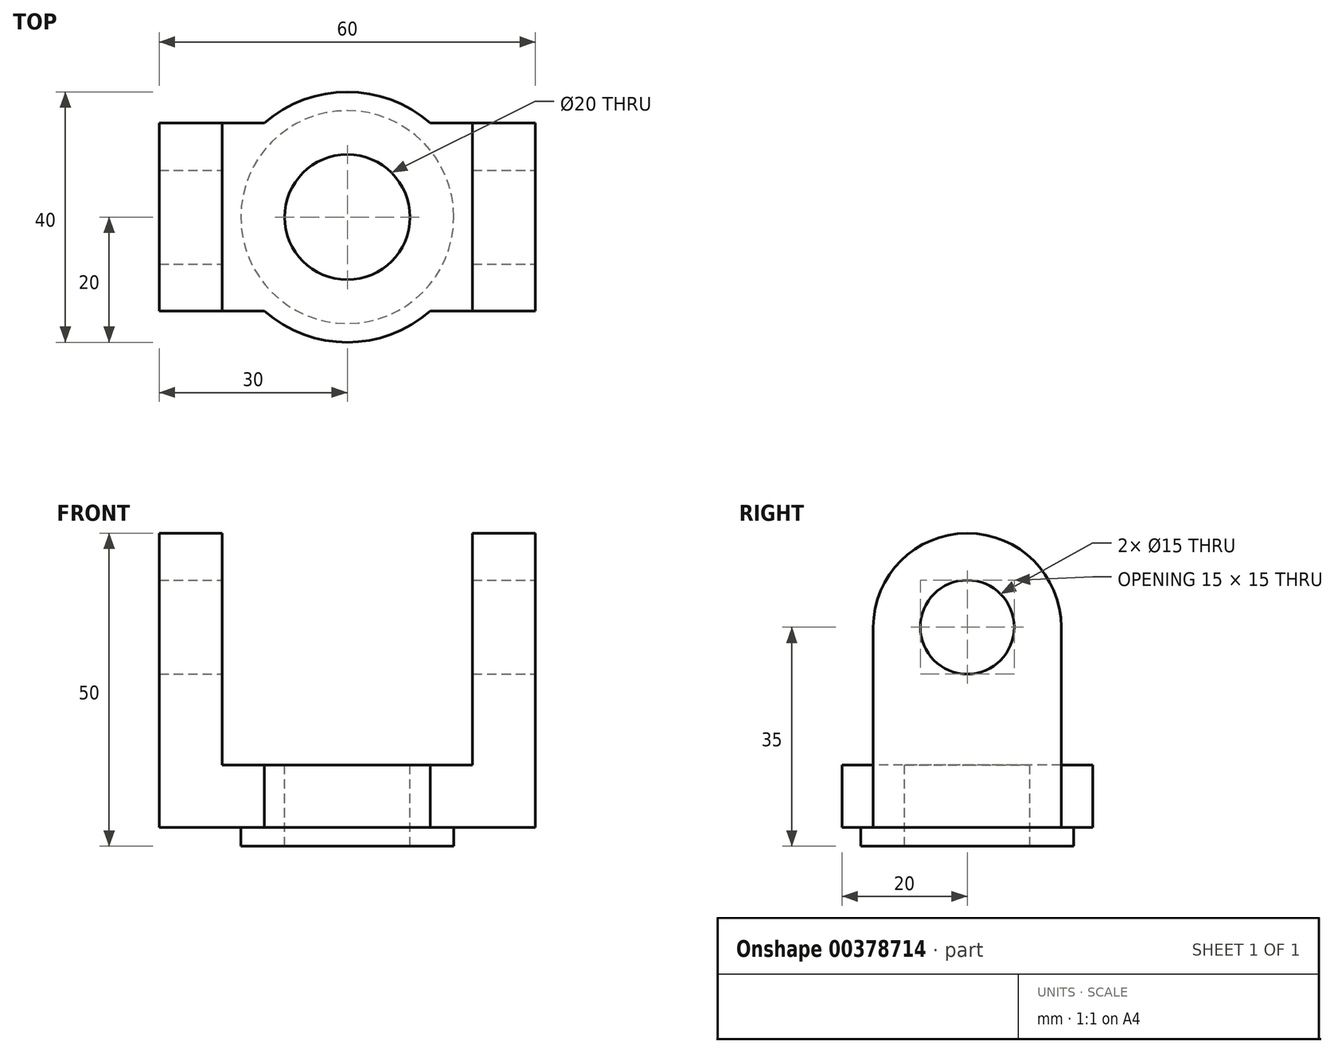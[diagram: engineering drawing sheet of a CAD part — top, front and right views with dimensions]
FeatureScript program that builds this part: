
annotation { "Feature Type Name" : "Feature", "Feature Type Description" : "" }
export const myFeature = defineFeature(function(context is Context, id is Id, definition is map)
    precondition{}
    {
        {
            var Q0;
            Q0=qCreatedBy(makeId("Top.planeOp"),FACE);
            var sketch = newSketch(context, id + "F0", { "sketchPlane" : qUnion([Q0])});
            skCircle(sketch, "E0", {"center": v(0, 0) * mm, "radius": 17 * mm});
            skSolve(sketch);
        }
        {
            var Q0;
            Q0 = qSketchRegion(id + "F0", true);
            extrude(context, id + "F1", {"entities" : qUnion([Q0]), "depth" : 3 * mm});
        }
        {
            var Q0;
            Q0=makeQuery(id+"F1.opExtrude","CAP_FACE",FACE,{"disambiguationData":[OSD([sQuery(id+"F0.wireOp",EDGE,"E0")])],"isStart":false});
            var sketch = newSketch(context, id + "F2", { "sketchPlane" : qUnion([Q0])});
            skLineSegment(sketch, "E1.bottom", {"start": v(-30, 15) * mm, "end": v(-13.23, 15) * mm});
            skLineSegment(sketch, "E1.top", {"start": v(-30, -15) * mm, "end": v(-13.23, -15) * mm});
            skLineSegment(sketch, "E1.left", {"start": v(-30, 15) * mm, "end": v(-30, -15) * mm});
            skLineSegment(sketch, "E1.right", {"start": v(30, 15) * mm, "end": v(30, -15) * mm});
            skLineSegment(sketch, "E2", {"start": v(0, 0) * mm, "end": v(0, 17) * mm, "construction": true});
            skLineSegment(sketch, "E3", {"start": v(0, 0) * mm, "end": v(17, 0) * mm, "construction": true});
            skArc(sketch, "E4", {"start": v(-13.23, -15) * mm, "mid": v(0, -20) * mm, "end": v(13.23, -15) * mm});
            skLineSegment(sketch, "E5.trimOffspring", {"start": v(13.23, 15) * mm, "end": v(30, 15) * mm});
            skLineSegment(sketch, "E6.trimOffspring", {"start": v(13.23, -15) * mm, "end": v(30, -15) * mm});
            skArc(sketch, "E7.trimOffspring", {"start": v(13.23, 15) * mm, "mid": v(0, 20) * mm, "end": v(-13.23, 15) * mm});
            skSolve(sketch);
        }
        {
            var Q0;
            Q0 = qSketchRegion(id + "F2", true);
            extrude(context, id + "F3", {"entities" : qUnion([Q0]), "operationType" : NewBodyOperationType.ADD, "depth" : 50 * mm});
        }
        {
            var Q0;
            Q0=makeQuery(id+"F3.opExtrude","SWEPT_FACE",FACE,{"disambiguationData":[OSD([sQuery(id+"F2.wireOp",EDGE,"E1.right")])]});
            var sketch = newSketch(context, id + "F4", { "sketchPlane" : qUnion([Q0])});
            skCircle(sketch, "E8", {"center": v(0, 35) * mm, "radius": 7.5 * mm});
            skArc(sketch, "E9", {"start": v(15, 35) * mm, "mid": v(0, 50) * mm, "end": v(-15, 35) * mm});
            skLineSegment(sketch, "E10", {"start": v(-15, 35) * mm, "end": v(-15, 53) * mm});
            skLineSegment(sketch, "E11", {"start": v(-15, 53) * mm, "end": v(15, 53) * mm});
            skLineSegment(sketch, "E12", {"start": v(15, 53) * mm, "end": v(15, 35) * mm});
            skSolve(sketch);
        }
        {
            var Q0;
            Q0 = qSketchRegion(id + "F4", true);
            extrude(context, id + "F5", {"entities" : qUnion([Q0]), "operationType" : NewBodyOperationType.REMOVE, "endBound" : BoundingType.THROUGH_ALL, "oppositeDirection" : true, "depth" : 25 * mm});
        }
        {
            var Q0;
            Q0=qCreatedBy(makeId("Front.planeOp"),FACE);
            var sketch = newSketch(context, id + "F6", { "sketchPlane" : qUnion([Q0])});
            skLineSegment(sketch, "E13.0.0", {"start": v(-13.23, 3) * mm, "end": v(13.23, 3) * mm});
            skLineSegment(sketch, "E13.0.1", {"start": v(13.23, 13) * mm, "end": v(13.23, 35) * mm});
            skLineSegment(sketch, "E13.0.2", {"start": v(13.23, 35) * mm, "end": v(13.23, 53) * mm});
            skLineSegment(sketch, "E13.0.3", {"start": v(13.23, 53) * mm, "end": v(-13.23, 53) * mm});
            skLineSegment(sketch, "E13.0.4", {"start": v(-13.23, 53) * mm, "end": v(-13.23, 35) * mm});
            skLineSegment(sketch, "E13.0.5", {"start": v(-13.23, 35) * mm, "end": v(-13.23, 13) * mm});
            skLineSegment(sketch, "E14", {"start": v(-13.23, 13) * mm, "end": v(13.23, 13) * mm});
            skLineSegment(sketch, "E15.bottom", {"start": v(-20, 53) * mm, "end": v(20, 53) * mm});
            skLineSegment(sketch, "E15.top", {"start": v(-20, 13) * mm, "end": v(20, 13) * mm});
            skLineSegment(sketch, "E15.left", {"start": v(-20, 53) * mm, "end": v(-20, 13) * mm});
            skLineSegment(sketch, "E15.right", {"start": v(20, 53) * mm, "end": v(20, 13) * mm});
            skLineSegment(sketch, "E16", {"start": v(0, 0) * mm, "end": v(0, 53) * mm, "construction": true});
            skSolve(sketch);
        }
        {
            var Q0;
            Q0 = qSketchRegion(id + "F6", true);
            extrude(context, id + "F7", {"entities" : qUnion([Q0]), "operationType" : NewBodyOperationType.REMOVE, "oppositeDirection" : true, "depth" : 25 * mm, "hasSecondDirection" : true, "secondDirectionOppositeDirection" : false, "secondDirectionDepth" : 25 * mm});
        }
        {
            var Q0;
            Q0=makeQuery(id+"F7.boolean.opBoolean","COPY",FACE,{"derivedFrom":makeQuery(id+"F7.opExtrude","SWEPT_FACE",FACE,{"disambiguationData":[OSD([sQuery(id+"F6.wireOp",EDGE,"E15.top")])]})});
            var sketch = newSketch(context, id + "F8", { "sketchPlane" : qUnion([Q0])});
            skCircle(sketch, "E17", {"center": v(0, 0) * mm, "radius": 10 * mm});
            skSolve(sketch);
        }
        {
            var Q0;
            Q0 = qSketchRegion(id + "F8", true);
            extrude(context, id + "F9", {"entities" : qUnion([Q0]), "operationType" : NewBodyOperationType.REMOVE, "endBound" : BoundingType.THROUGH_ALL, "oppositeDirection" : true, "depth" : 25 * mm});
        }
    });
